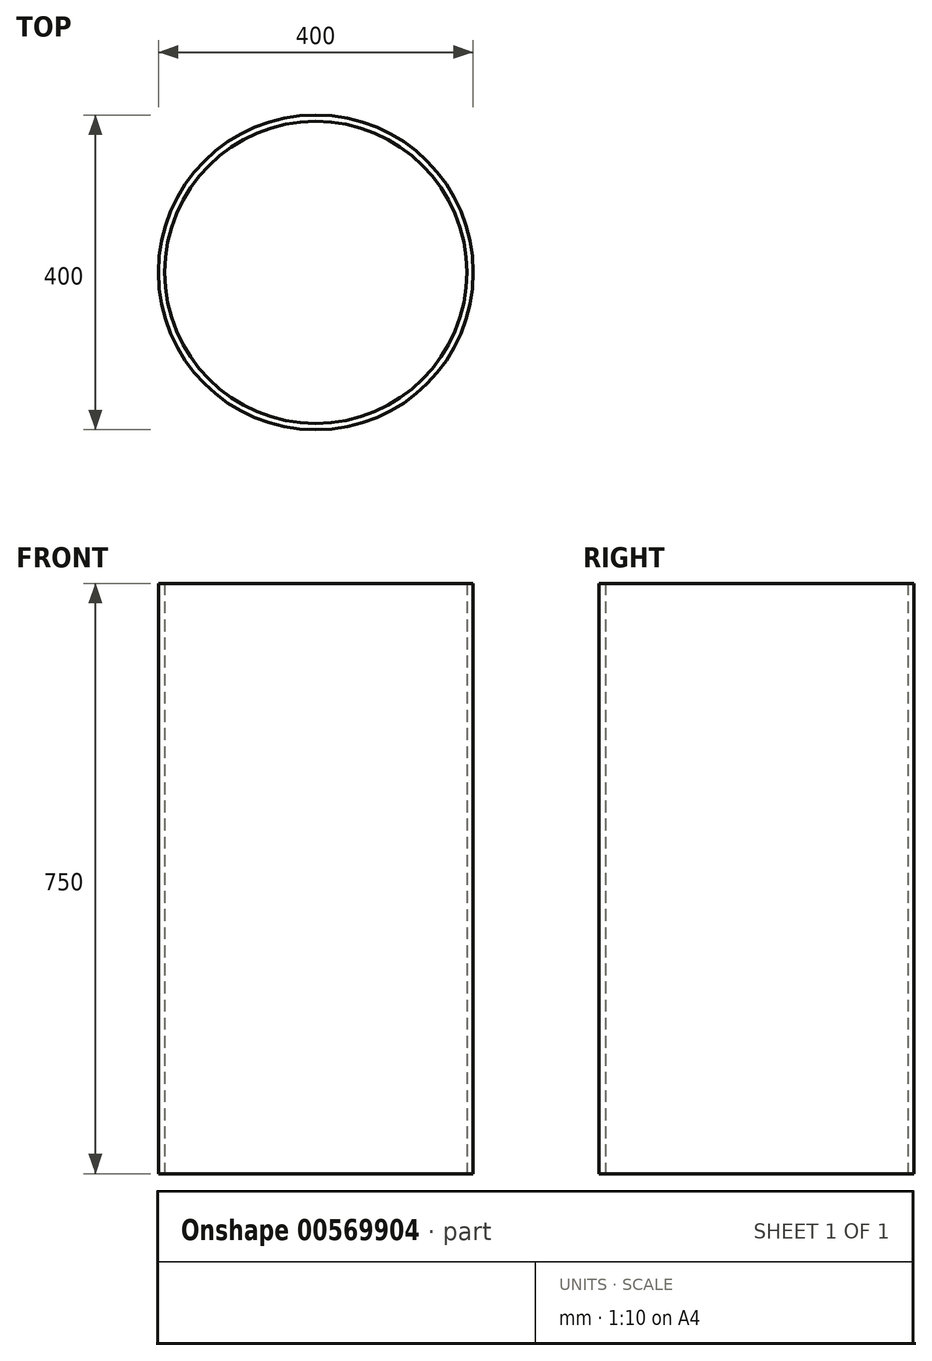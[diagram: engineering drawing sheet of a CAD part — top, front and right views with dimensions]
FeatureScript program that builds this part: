
annotation { "Feature Type Name" : "Feature", "Feature Type Description" : "" }
export const myFeature = defineFeature(function(context is Context, id is Id, definition is map)
    precondition{}
    {
        {
            var Q0;
            Q0=qCreatedBy(makeId("Top.planeOp"),FACE);
            var sketch = newSketch(context, id + "F0", { "sketchPlane" : qUnion([Q0])});
            skCircle(sketch, "E0", {"center": v(0, 0) * mm, "radius": 200 * mm});
            skCircle(sketch, "E1", {"center": v(0, 0) * mm, "radius": 192 * mm});
            skSolve(sketch);
        }
        {
            var Q0;
            Q0=qSketchRegion(id+"F0",true);
            extrude(context, id + "F1", {"entities" : qUnion([Q0]), "depth" : 750 * mm, "offsetDistance" : 25 * mm});
        }
    });
